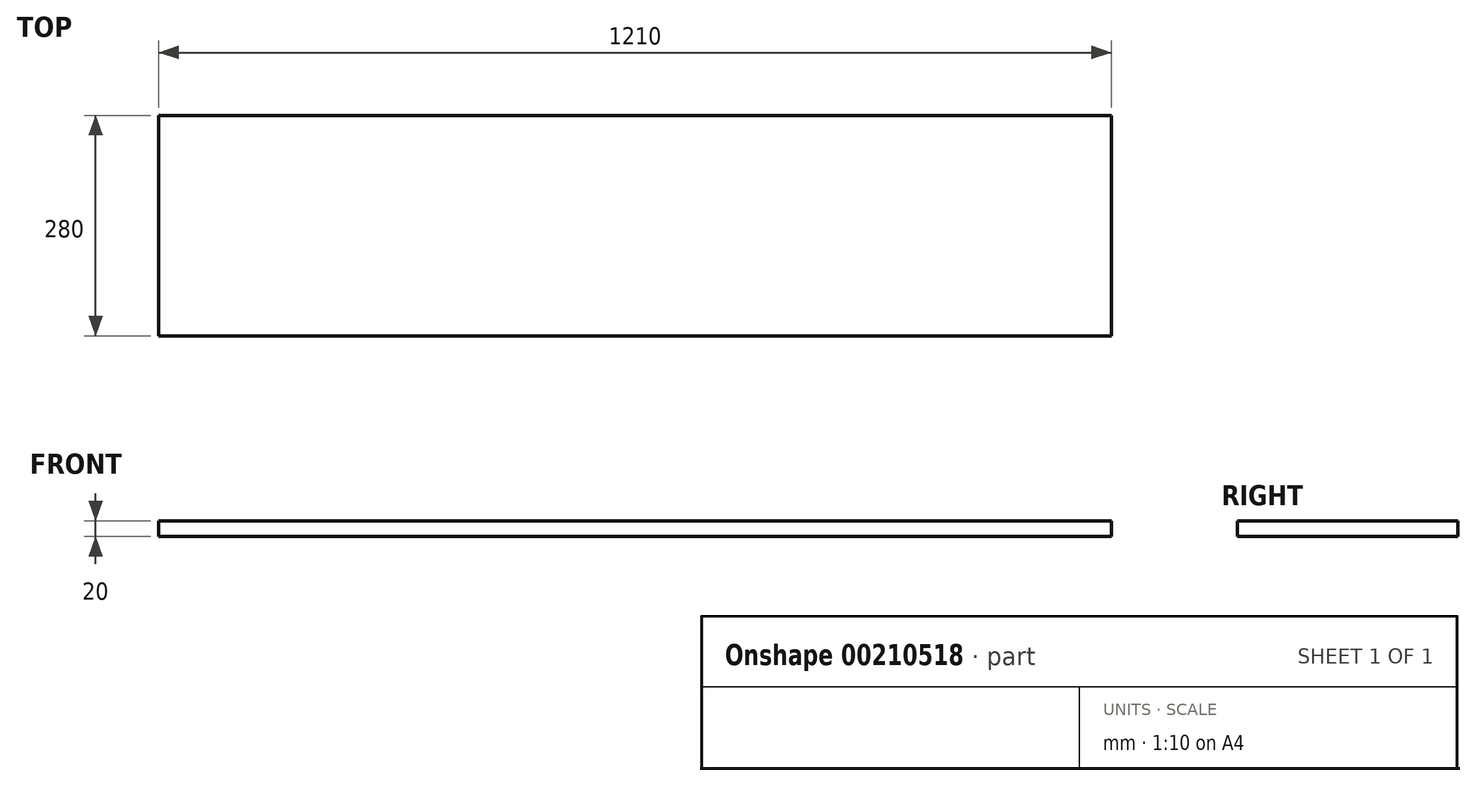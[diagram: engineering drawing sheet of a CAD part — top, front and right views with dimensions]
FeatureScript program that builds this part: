
annotation { "Feature Type Name" : "Feature", "Feature Type Description" : "" }
export const myFeature = defineFeature(function(context is Context, id is Id, definition is map)
    precondition{}
    {
        {
            var Q0;
            Q0=qCreatedBy(makeId("Top.planeOp"),FACE);
            var sketch = newSketch(context, id + "F0", { "sketchPlane" : qUnion([Q0])});
            skLineSegment(sketch, "E0.bottom", {"start": v(-607.4, -240.24) * mm, "end": v(602.6, -240.24) * mm});
            skLineSegment(sketch, "E0.top", {"start": v(-607.4, -520.24) * mm, "end": v(602.6, -520.24) * mm});
            skLineSegment(sketch, "E0.left", {"start": v(-607.4, -240.24) * mm, "end": v(-607.4, -520.24) * mm});
            skLineSegment(sketch, "E0.right", {"start": v(602.6, -240.24) * mm, "end": v(602.6, -520.24) * mm});
            skSolve(sketch);
        }
        {
            var Q0;
            Q0 = qSketchRegion(id + "F0", true);
            var Q1;
            Q1=makeQuery(id+"F0.imprint","IMPRINT",FACE,{"disambiguationData":[TD([[makeQuery(id+"F0.imprint","IMPRINT",EDGE,{"derivedFrom":sQuery(id+"F0.wireOp",EDGE,"E0.bottom")}),-1.0]])]});
            extrude(context, id + "F1", {"entities" : qUnion([Q0, Q1]), "depth" : 20 * mm});
        }
    });
